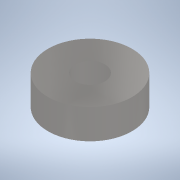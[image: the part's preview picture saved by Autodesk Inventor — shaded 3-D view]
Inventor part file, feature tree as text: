
AUTODESK INVENTOR PART (.ipt)
format: ipt  version: 2020.3 (Build 243373000, 373)  size: 133,632 bytes
history: native  units: mm
features: other x1, extrude x1, fillet x1, sketch x1
ambient origin geometry x8: Origin, YZ Plane, XZ Plane, XY Plane, X Axis, Y Axis, Z Axis, Center Point
bodies: Body1 (feature_tree)
feature tree (4):
  other  "ソリッド1"
  extrude  "押し出し1"  Depth=17.0mm
  fillet  "フィレット1"  Radius=6.0mm
  sketch  "スケッチ1"
